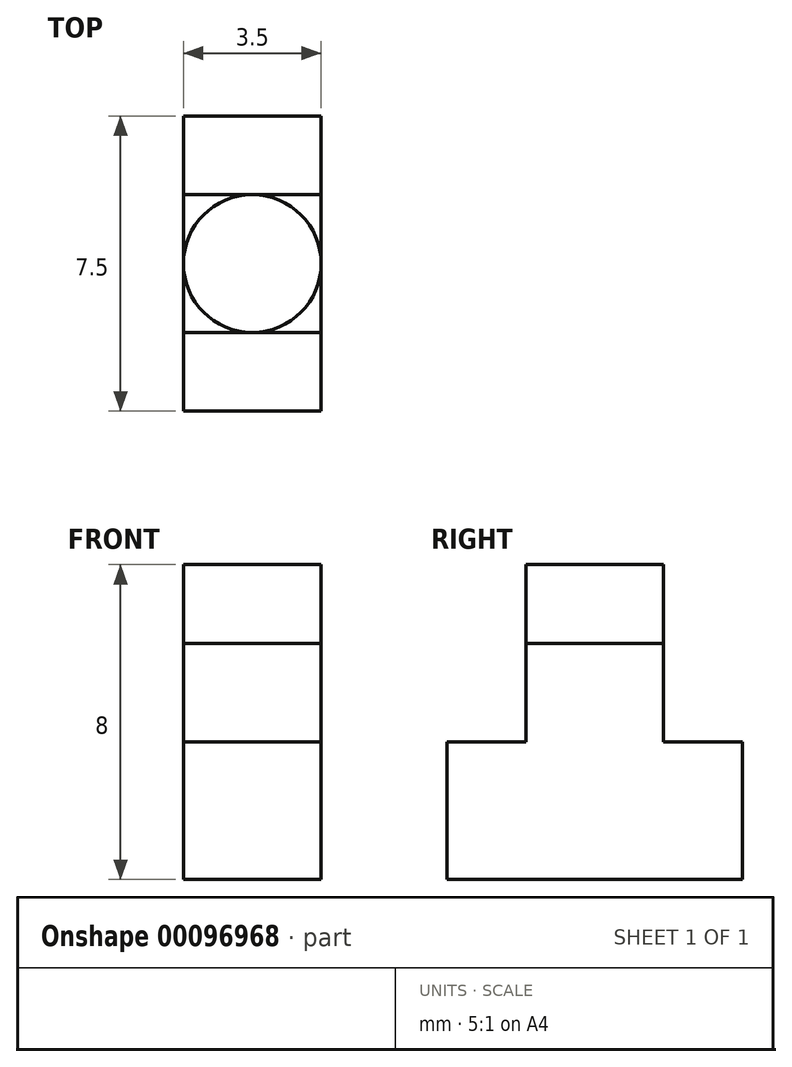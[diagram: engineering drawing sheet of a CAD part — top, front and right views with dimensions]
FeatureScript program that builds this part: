
annotation { "Feature Type Name" : "Feature", "Feature Type Description" : "" }
export const myFeature = defineFeature(function(context is Context, id is Id, definition is map)
    precondition{}
    {
        {
            var Q0;
            Q0=qCreatedBy(makeId("Top.planeOp"),FACE);
            var sketch = newSketch(context, id + "F0", { "sketchPlane" : qUnion([Q0])});
            skLineSegment(sketch, "E0.bottom", {"start": v(1.75, -3.75) * mm, "end": v(-1.75, -3.75) * mm});
            skLineSegment(sketch, "E0.top", {"start": v(1.75, 3.75) * mm, "end": v(-1.75, 3.75) * mm});
            skLineSegment(sketch, "E0.left", {"start": v(1.75, -3.75) * mm, "end": v(1.75, 3.75) * mm});
            skLineSegment(sketch, "E0.right", {"start": v(-1.75, -3.75) * mm, "end": v(-1.75, 3.75) * mm});
            skPoint(sketch, "E0.middle", {"position": v(0, 0) * mm});
            skLineSegment(sketch, "E1.bottom", {"start": v(1.75, -1.75) * mm, "end": v(-1.9, -1.75) * mm});
            skLineSegment(sketch, "E1.top", {"start": v(1.9, 1.75) * mm, "end": v(-1.75, 1.75) * mm});
            skLineSegment(sketch, "E2", {"start": v(1.75, -1.75) * mm, "end": v(-1.75, 0) * mm});
            skLineSegment(sketch, "E3", {"start": v(-1.75, 0) * mm, "end": v(1.75, 1.75) * mm});
            skCircle(sketch, "E4", {"center": v(0, 0) * mm, "radius": 1.75 * mm});
            skSolve(sketch);
        }
        {
            var Q0;
            {var subQ0=sQuery(id+"F0.wireOp",EDGE,"E1.bottom");var subQ1=sQuery(id+"F0.wireOp",EDGE,"E0.left");var subQ2=makeQuery(id+"F0.imprint","INTERSECT",VERTEX,{"derivedFrom":[subQ1,subQ0]});Q0=makeQuery(id+"F0.imprint","IMPRINT",FACE,{"disambiguationData":[TD([[makeQuery(id+"F0.imprint","IMPRINT",EDGE,{"disambiguationData":[TD([[subQ2,-1.0]])],"derivedFrom":subQ1}),1.0]])]});}
            var Q1;
            {var subQ0=sQuery(id+"F0.wireOp",EDGE,"E0.top");Q1=makeQuery(id+"F0.imprint","IMPRINT",FACE,{"disambiguationData":[TD([[makeQuery(id+"F0.imprint","IMPRINT",EDGE,{"derivedFrom":subQ0}),1.0]])]});}
            var Q2;
            {var subQ0=sQuery(id+"F0.wireOp",EDGE,"E0.bottom");Q2=makeQuery(id+"F0.imprint","IMPRINT",FACE,{"disambiguationData":[TD([[makeQuery(id+"F0.imprint","IMPRINT",EDGE,{"derivedFrom":subQ0}),-1.0]])]});}
            var Q3;
            {var subQ0=sQuery(id+"F0.wireOp",EDGE,"E2");Q3=makeQuery(id+"F0.imprint","IMPRINT",FACE,{"disambiguationData":[TD([[makeQuery(id+"F0.imprint","IMPRINT",EDGE,{"derivedFrom":subQ0}),1.0]])]});}
            var Q4;
            {var subQ3=sQuery(id+"F0.wireOp",EDGE,"E3");Q4=makeQuery(id+"F0.imprint","IMPRINT",FACE,{"disambiguationData":[TD([[makeQuery(id+"F0.imprint","IMPRINT",EDGE,{"derivedFrom":subQ3}),1.0]])]});}
            var Q5;
            {var subQ1=sQuery(id+"F0.wireOp",EDGE,"E0.right");var subQ3=sQuery(id+"F0.wireOp",EDGE,"E1.bottom");var subQ4=makeQuery(id+"F0.imprint","INTERSECT",VERTEX,{"derivedFrom":[subQ1,subQ3]});Q5=makeQuery(id+"F0.imprint","IMPRINT",FACE,{"disambiguationData":[TD([[makeQuery(id+"F0.imprint","IMPRINT",EDGE,{"disambiguationData":[TD([[subQ4,1.0]])],"derivedFrom":subQ3}),-1.0]])]});}
            var Q6;
            {var subQ0=sQuery(id+"F0.wireOp",EDGE,"E4");var subQ6=makeQuery(id+"F0.imprint","INTERSECT",VERTEX,{"derivedFrom":[sQuery(id+"F0.wireOp",EDGE,"E0.left"),subQ0]});Q6=makeQuery(id+"F0.imprint","IMPRINT",FACE,{"disambiguationData":[TD([[makeQuery(id+"F0.imprint","IMPRINT",EDGE,{"disambiguationData":[TD([[subQ6,-1.0]])],"derivedFrom":subQ0}),1.0]])]});}
            var Q7;
            {var subQ0=sQuery(id+"F0.wireOp",EDGE,"E1.top");var subQ1=sQuery(id+"F0.wireOp",EDGE,"E0.right");var subQ2=makeQuery(id+"F0.imprint","INTERSECT",VERTEX,{"derivedFrom":[subQ1,subQ0]});Q7=makeQuery(id+"F0.imprint","IMPRINT",FACE,{"disambiguationData":[TD([[makeQuery(id+"F0.imprint","IMPRINT",EDGE,{"disambiguationData":[TD([[subQ2,1.0]])],"derivedFrom":subQ0}),1.0]])]});}
            var Q8;
            {var subQ1=sQuery(id+"F0.wireOp",EDGE,"E0.left");var subQ3=sQuery(id+"F0.wireOp",EDGE,"E4");var subQ4=makeQuery(id+"F0.imprint","INTERSECT",VERTEX,{"derivedFrom":[subQ1,subQ3]});Q8=makeQuery(id+"F0.imprint","IMPRINT",FACE,{"disambiguationData":[TD([[makeQuery(id+"F0.imprint","IMPRINT",EDGE,{"disambiguationData":[TD([[subQ4,-1.0]])],"derivedFrom":subQ3}),-1.0]])]});}
            extrude(context, id + "F1", {"entities" : qUnion([Q0, Q1, Q2, Q3, Q4, Q5, Q6, Q7, Q8]), "depth" : 3.5 * mm});
        }
        {
            var Q0;
            {var subQ0=sQuery(id+"F0.wireOp",EDGE,"E4");var subQ6=makeQuery(id+"F0.imprint","INTERSECT",VERTEX,{"derivedFrom":[sQuery(id+"F0.wireOp",EDGE,"E0.left"),subQ0]});Q0=makeQuery(id+"F0.imprint","IMPRINT",FACE,{"disambiguationData":[TD([[makeQuery(id+"F0.imprint","IMPRINT",EDGE,{"disambiguationData":[TD([[subQ6,-1.0]])],"derivedFrom":subQ0}),1.0]])]});}
            var Q1;
            {var subQ0=sQuery(id+"F0.wireOp",EDGE,"E4");var subQ4=makeQuery(id+"F0.imprint","INTERSECT",VERTEX,{"derivedFrom":[sQuery(id+"F0.wireOp",EDGE,"E1.bottom"),subQ0]});Q1=makeQuery(id+"F0.imprint","IMPRINT",FACE,{"disambiguationData":[TD([[makeQuery(id+"F0.imprint","IMPRINT",EDGE,{"disambiguationData":[TD([[subQ4,-1.0]])],"derivedFrom":subQ0}),1.0]])]});}
            var Q2;
            {var subQ0=sQuery(id+"F0.wireOp",EDGE,"E4");var subQ4=makeQuery(id+"F0.imprint","INTERSECT",VERTEX,{"derivedFrom":[sQuery(id+"F0.wireOp",EDGE,"E1.top"),subQ0]});Q2=makeQuery(id+"F0.imprint","IMPRINT",FACE,{"disambiguationData":[TD([[makeQuery(id+"F0.imprint","IMPRINT",EDGE,{"disambiguationData":[TD([[subQ4,1.0]])],"derivedFrom":subQ0}),1.0]])]});}
            extrude(context, id + "F2", {"entities" : qUnion([Q0, Q1, Q2]), "operationType" : NewBodyOperationType.ADD, "depth" : 8 * mm});
        }
        {
            var Q0;
            {var subQ0=sQuery(id+"F0.wireOp",EDGE,"E2");Q0=makeQuery(id+"F0.imprint","IMPRINT",FACE,{"disambiguationData":[TD([[makeQuery(id+"F0.imprint","IMPRINT",EDGE,{"derivedFrom":subQ0}),1.0]])]});}
            var Q1;
            {var subQ3=sQuery(id+"F0.wireOp",EDGE,"E3");Q1=makeQuery(id+"F0.imprint","IMPRINT",FACE,{"disambiguationData":[TD([[makeQuery(id+"F0.imprint","IMPRINT",EDGE,{"derivedFrom":subQ3}),1.0]])]});}
            var Q2;
            {var subQ1=sQuery(id+"F0.wireOp",EDGE,"E0.left");var subQ3=sQuery(id+"F0.wireOp",EDGE,"E4");var subQ4=makeQuery(id+"F0.imprint","INTERSECT",VERTEX,{"derivedFrom":[subQ1,subQ3]});Q2=makeQuery(id+"F0.imprint","IMPRINT",FACE,{"disambiguationData":[TD([[makeQuery(id+"F0.imprint","IMPRINT",EDGE,{"disambiguationData":[TD([[subQ4,1.0]])],"derivedFrom":subQ3}),-1.0]])]});}
            var Q3;
            {var subQ1=sQuery(id+"F0.wireOp",EDGE,"E0.left");var subQ3=sQuery(id+"F0.wireOp",EDGE,"E4");var subQ4=makeQuery(id+"F0.imprint","INTERSECT",VERTEX,{"derivedFrom":[subQ1,subQ3]});Q3=makeQuery(id+"F0.imprint","IMPRINT",FACE,{"disambiguationData":[TD([[makeQuery(id+"F0.imprint","IMPRINT",EDGE,{"disambiguationData":[TD([[subQ4,-1.0]])],"derivedFrom":subQ3}),-1.0]])]});}
            var Q4;
            {var subQ1=sQuery(id+"F0.wireOp",EDGE,"E0.right");var subQ3=sQuery(id+"F0.wireOp",EDGE,"E1.bottom");var subQ4=makeQuery(id+"F0.imprint","INTERSECT",VERTEX,{"derivedFrom":[subQ1,subQ3]});Q4=makeQuery(id+"F0.imprint","IMPRINT",FACE,{"disambiguationData":[TD([[makeQuery(id+"F0.imprint","IMPRINT",EDGE,{"disambiguationData":[TD([[subQ4,1.0]])],"derivedFrom":subQ3}),-1.0]])]});}
            var Q5;
            {var subQ0=sQuery(id+"F0.wireOp",EDGE,"E1.top");var subQ1=sQuery(id+"F0.wireOp",EDGE,"E0.right");var subQ2=makeQuery(id+"F0.imprint","INTERSECT",VERTEX,{"derivedFrom":[subQ1,subQ0]});Q5=makeQuery(id+"F0.imprint","IMPRINT",FACE,{"disambiguationData":[TD([[makeQuery(id+"F0.imprint","IMPRINT",EDGE,{"disambiguationData":[TD([[subQ2,1.0]])],"derivedFrom":subQ0}),1.0]])]});}
            extrude(context, id + "F3", {"entities" : qUnion([Q0, Q1, Q2, Q3, Q4, Q5]), "operationType" : NewBodyOperationType.ADD, "depth" : 6 * mm});
        }
    });
